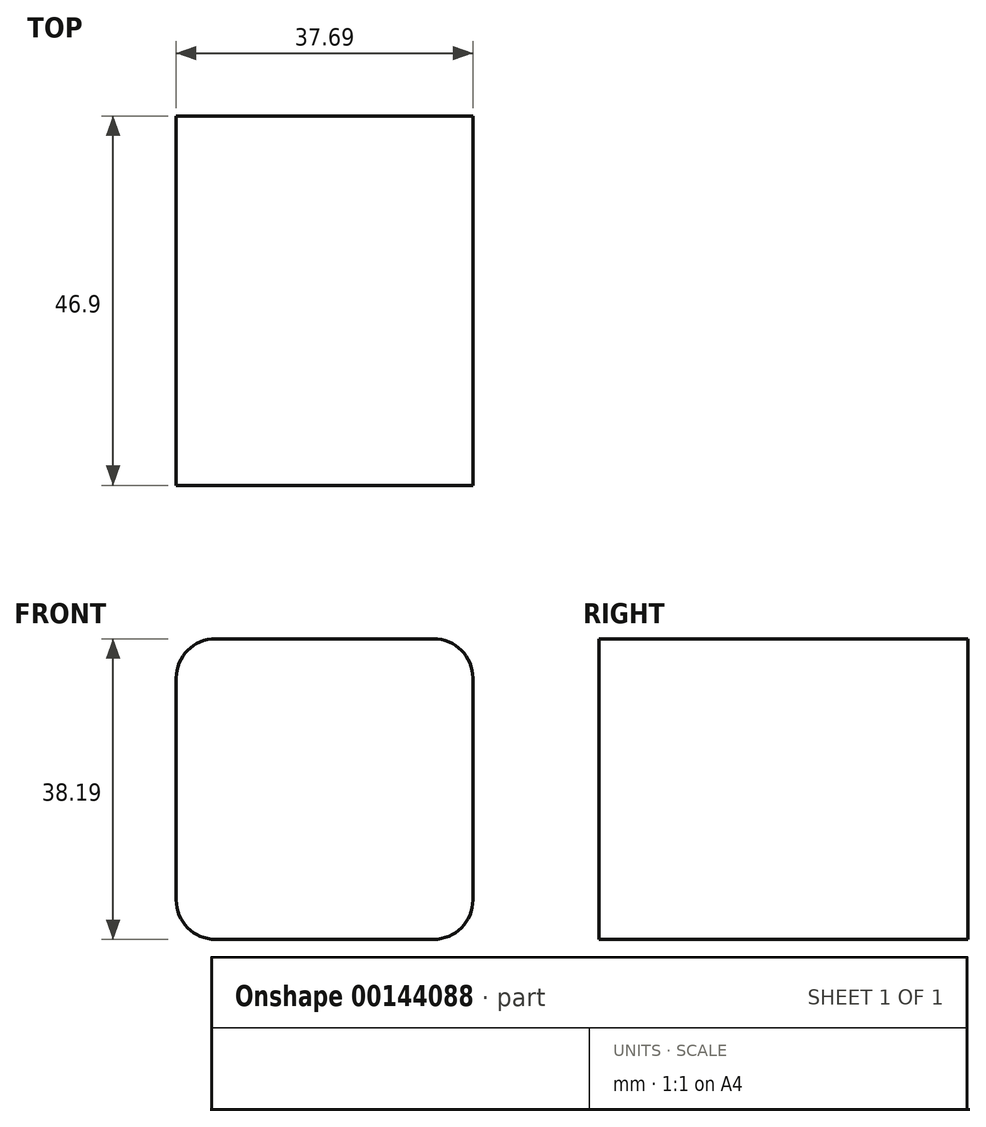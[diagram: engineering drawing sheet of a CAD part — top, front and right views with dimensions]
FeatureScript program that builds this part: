
annotation { "Feature Type Name" : "Feature", "Feature Type Description" : "" }
export const myFeature = defineFeature(function(context is Context, id is Id, definition is map)
    precondition{}
    {
        {
            var Q0;
            Q0=qCreatedBy(makeId("Front.planeOp"),FACE);
            var sketch = newSketch(context, id + "F0", { "sketchPlane" : qUnion([Q0])});
            skLineSegment(sketch, "E0", {"start": v(-12.26, 15.14) * mm, "end": v(15.43, 15.14) * mm});
            skLineSegment(sketch, "E1", {"start": v(20.43, 10.14) * mm, "end": v(20.43, -18.05) * mm});
            skLineSegment(sketch, "E2", {"start": v(15.43, -23.05) * mm, "end": v(-12.26, -23.05) * mm});
            skLineSegment(sketch, "E3", {"start": v(-17.26, -18.05) * mm, "end": v(-17.26, 10.14) * mm});
            skPoint(sketch, "E4.visualSharp", {"position": v(-17.26, 15.14) * mm});
            skArc(sketch, "E4.filletArc", {"start": v(-12.26, 15.14) * mm, "mid": v(-15.8, 13.67) * mm, "end": v(-17.26, 10.14) * mm});
            skPoint(sketch, "E5.visualSharp", {"position": v(20.43, 15.14) * mm});
            skArc(sketch, "E5.filletArc", {"start": v(20.43, 10.14) * mm, "mid": v(18.97, 13.67) * mm, "end": v(15.43, 15.14) * mm});
            skPoint(sketch, "E6.visualSharp", {"position": v(20.43, -23.05) * mm});
            skArc(sketch, "E6.filletArc", {"start": v(15.43, -23.05) * mm, "mid": v(18.97, -21.58) * mm, "end": v(20.43, -18.05) * mm});
            skPoint(sketch, "E7.visualSharp", {"position": v(-17.26, -23.05) * mm});
            skArc(sketch, "E7.filletArc", {"start": v(-17.26, -18.05) * mm, "mid": v(-15.8, -21.58) * mm, "end": v(-12.26, -23.05) * mm});
            skSolve(sketch);
        }
        {
            var Q0;
            Q0 = qSketchRegion(id + "F0", true);
            extrude(context, id + "F1", {"entities" : qUnion([Q0]), "depth" : 46.9 * mm, "offsetDistance" : 25 * mm});
        }
    });
